# Revit family: KEUCO_14962010000_
name_source: partatom
category: Specialty Equipment
revit_build: Autodesk Revit 2016 (Build: 20150220_1215(x64)
units: mm (PartAtom-declared; Revit-internal decimal feet)

## family parameters
Always vertical = Yes
Cut with Voids When Loaded = No
Part Type = Normal
Room Calculation Point = No
Round Connector Dimension = Use Diameter
Shared = No
Work Plane-Based = No

## types (3) — shared parameters
Breite = 129 mm  [stored 0.423228 ft]
Description = kleine Ausführung
Gewicht = 382
Kategorie = ACC
Manufacturer = KEUCO
Preisgruppe = 1
Serie = Plan
URL = https://www.keuco.com
Verwendung = GWC / WC

## per-type parameters (varying)
| type | Artikelnummer | Ausschreibungstext |
| 14962010000 | 14922010000 | KEUCO PLAN Handtuchring 14922010000
Hochglanzverchromter Handtuchring 
in ästhetischem, funktionalem Design
kleine Ausführung, offene, rechteckige Form
Ring schwenkbar, antistatisch, leicht zu reinigen
Breite 179 mm, Höhe 105 mm
Der Handtuchring wird verdeckt angebracht
Lieferung inkl. korrosionsfreiem Befestigungsmaterial |
| 14962070000 | 14922070000 | KEUCO PLAN Handtuchring 14922070000
Handtuchring aus hochwertigem Edelstahl 
in ästhetischem, funktionalem Design
kleine Ausführung, offene, rechteckige Form
Ring schwenkbar, antistatisch, leicht zu reinigen
Breite 179 mm, Höhe 105 mm
Der Handtuchring wird verdeckt angebracht
Lieferung inkl. korrosionsfreiem Befestigungsmaterial |
| 14962170000 | 14922170000 | KEUCO PLAN Handtuchring 14922170000
Handtuchring aus 
elegantem silber-eloxierten Aluminium (E6 EV1)/verchromt, 
in ästhetischem, funktionalem Design
kleine Ausführung, offene, rechteckige Form
Ring schwenkbar, antistatisch, leicht zu reinigen
Die Wandhalterung ist als Design-Element hochglanzverchromt
Breite 179 mm, Höhe 105 mm
Der Handtuchring wird verdeckt angebracht
Lieferung inkl. korrosionsfreiem Befestigungsmaterial |

note: [stored X ft] marks values corroborated as IEEE doubles in the binary element streams (Revit-internal decimal feet)

## geometry (parser evidence)
native form markers: Blend x4, Sweep x2
no freeform markers — native parametric forms only
